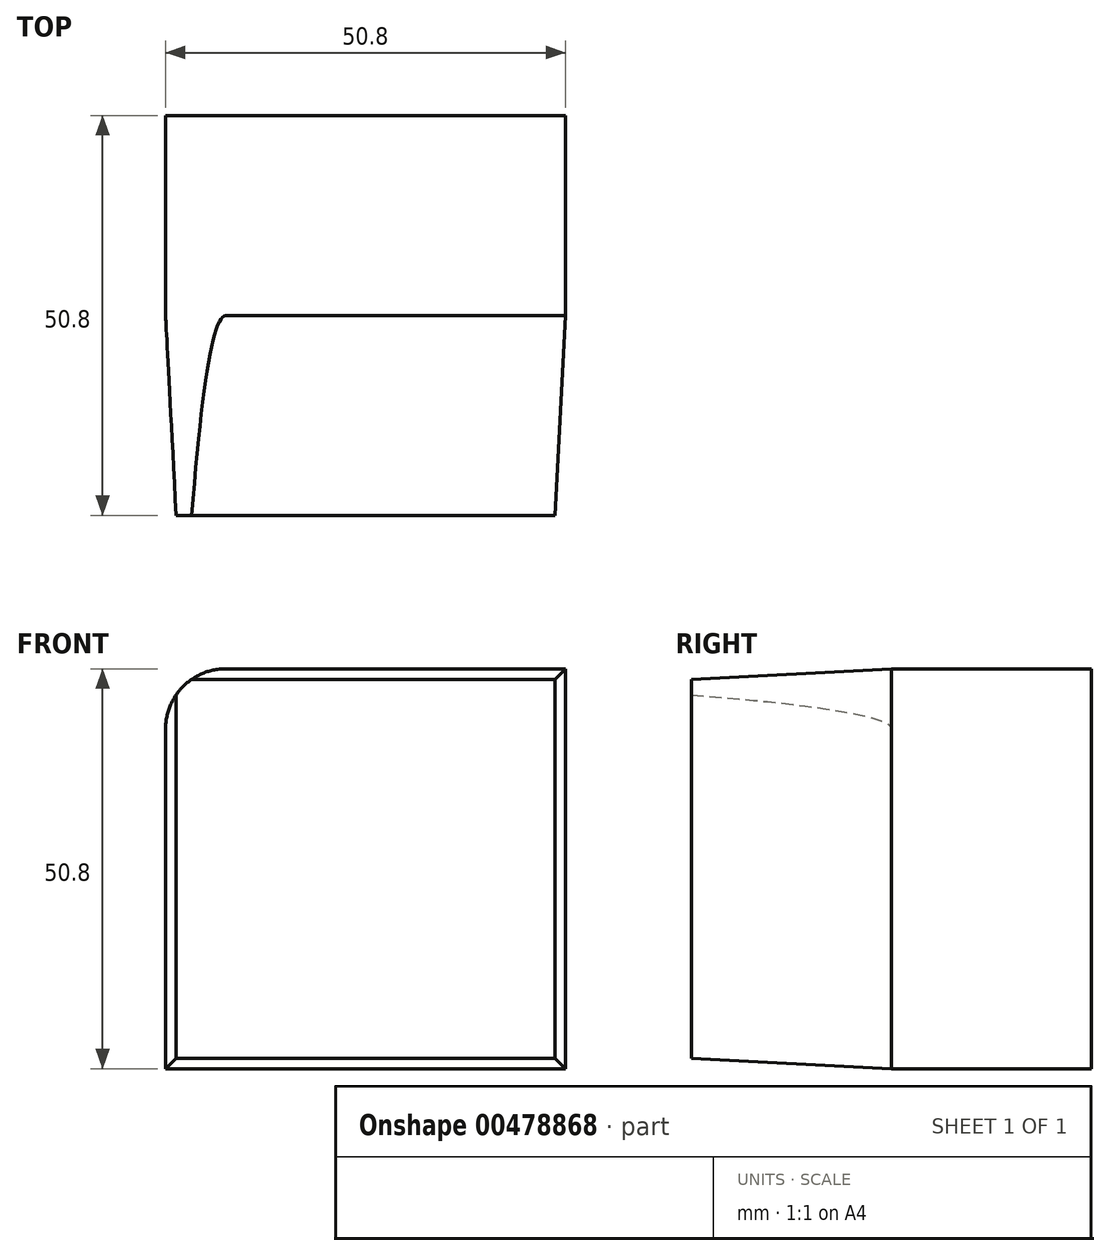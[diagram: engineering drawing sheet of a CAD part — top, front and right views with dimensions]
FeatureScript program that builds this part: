
annotation { "Feature Type Name" : "Feature", "Feature Type Description" : "" }
export const myFeature = defineFeature(function(context is Context, id is Id, definition is map)
    precondition{}
    {
        {
            var Q0;
            Q0=qCreatedBy(makeId("Front.planeOp"),FACE);
            var sketch = newSketch(context, id + "F0", { "sketchPlane" : qUnion([Q0])});
            skLineSegment(sketch, "E0.bottom", {"start": v(25.4, -25.4) * mm, "end": v(-25.4, -25.4) * mm});
            skLineSegment(sketch, "E0.top", {"start": v(25.4, 25.4) * mm, "end": v(-25.4, 25.4) * mm});
            skLineSegment(sketch, "E0.left", {"start": v(25.4, -25.4) * mm, "end": v(25.4, 25.4) * mm});
            skLineSegment(sketch, "E0.right", {"start": v(-25.4, -25.4) * mm, "end": v(-25.4, 25.4) * mm});
            skPoint(sketch, "E0.middle", {"position": v(0, 0) * mm});
            skSolve(sketch);
        }
        {
            var Q0;
            Q0 = qSketchRegion(id + "F0", true);
            extrude(context, id + "F1", {"entities" : qUnion([Q0]), "depth" : 25.4 * mm, "hasDraft" : true, "draftAngle" : 3 * degree, "draftPullDirection" : true, "hasSecondDirection" : true, "secondDirectionOppositeDirection" : true, "secondDirectionDepth" : 25.4 * mm});
        }
        {
            var Q0;
            Q0=makeQuery(id+"F1.*.split.splitOp","SPLIT",EDGE,{"derivedFrom":makeQuery(id+"F1.opExtrude","SWEPT_EDGE",EDGE,{"disambiguationData":[OSD([sQuery(id+"F0.wireOp",EDGE,"E0.top"),sQuery(id+"F0.wireOp",EDGE,"E0.right")])]}),"isFromBackBody":true});
            fillet(context, id + "F2", {"entities" : qUnion([Q0]), "radius" : 7.62 * mm, "tangentPropagation" : true, "allowEdgeOverflow" : false});
        }
    });
